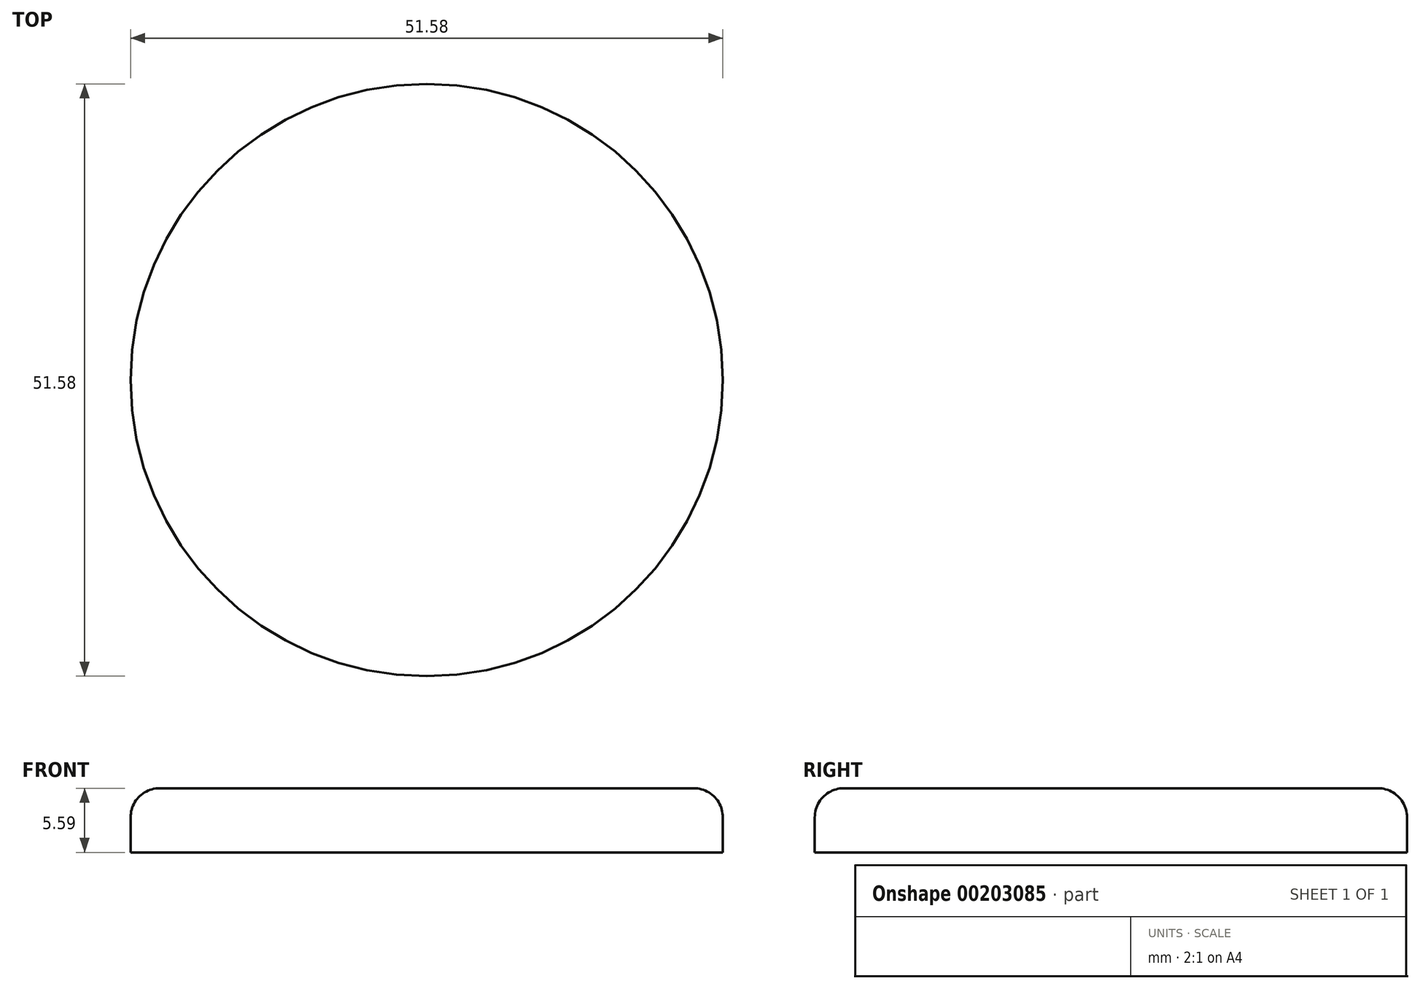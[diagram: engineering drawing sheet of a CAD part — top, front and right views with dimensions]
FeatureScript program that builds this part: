
annotation { "Feature Type Name" : "Feature", "Feature Type Description" : "" }
export const myFeature = defineFeature(function(context is Context, id is Id, definition is map)
    precondition{}
    {
        {
            var Q0;
            Q0=qCreatedBy(makeId("Top.planeOp"),FACE);
            var sketch = newSketch(context, id + "F0", { "sketchPlane" : qUnion([Q0])});
            skCircle(sketch, "E0", {"center": v(-11.53, 0) * mm, "radius": 25.79 * mm});
            skSolve(sketch);
        }
        {
            var Q0;
            Q0 = qSketchRegion(id + "F0", true);
            extrude(context, id + "F1", {"entities" : qUnion([Q0]), "depth" : 5.6 * mm});
        }
        {
            var Q0;
            Q0=makeQuery(id+"F1.opExtrude","CAP_FACE",FACE,{"disambiguationData":[OSD([sQuery(id+"F0.wireOp",EDGE,"E0")])],"isStart":false});
            fillet(context, id + "F2", {"entities" : qUnion([Q0]), "radius" : 2.54 * mm, "tangentPropagation" : true, "allowEdgeOverflow" : false});
        }
    });
